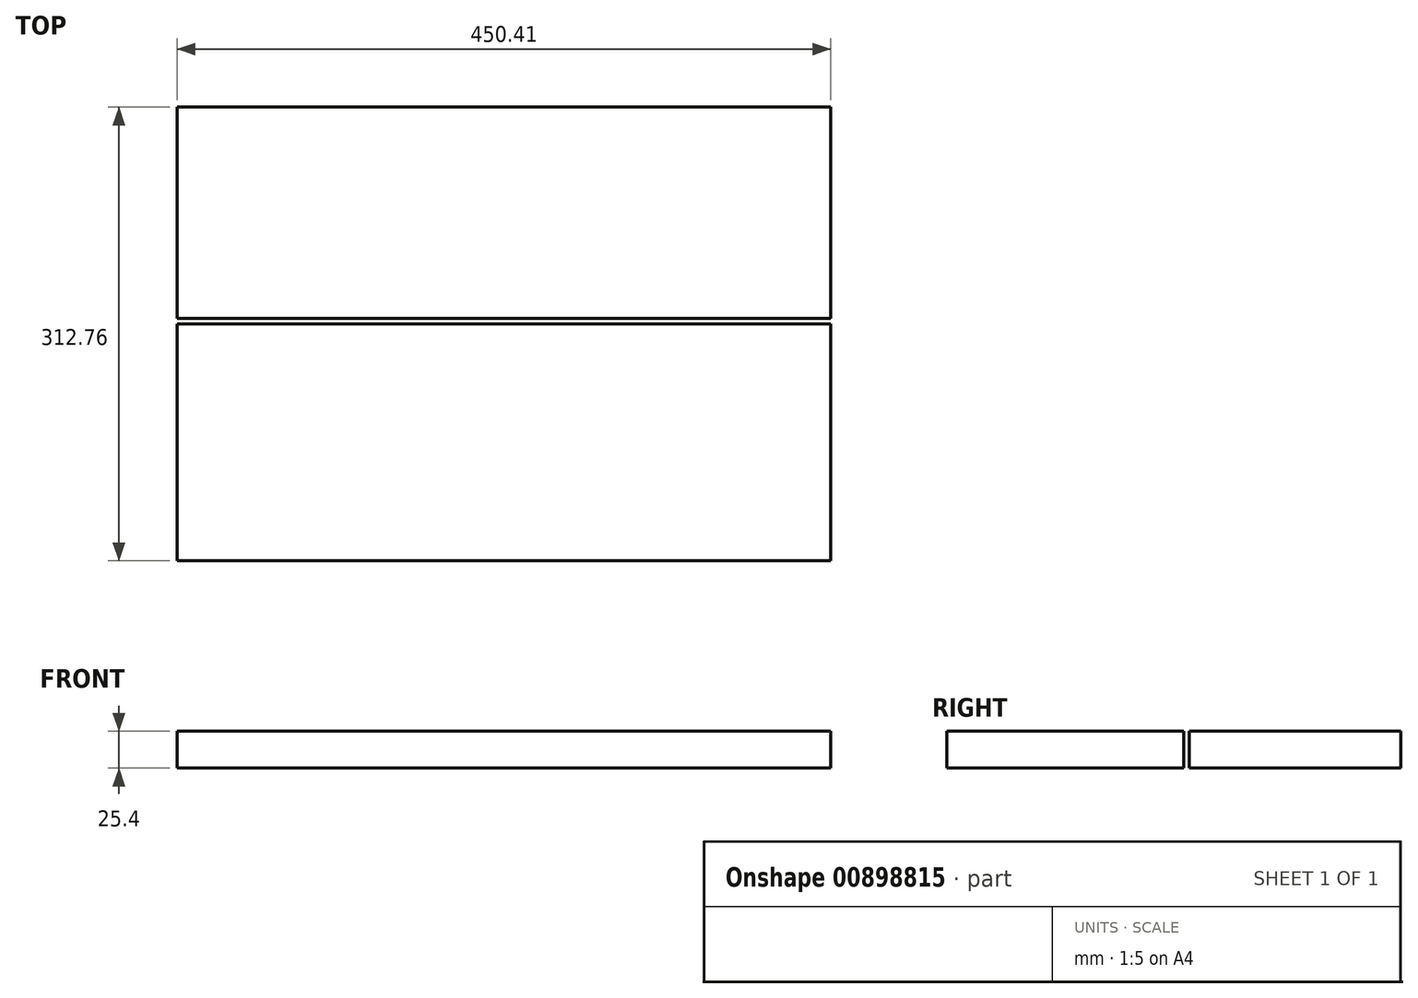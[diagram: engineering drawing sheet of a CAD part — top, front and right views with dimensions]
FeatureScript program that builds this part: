
annotation { "Feature Type Name" : "Feature", "Feature Type Description" : "" }
export const myFeature = defineFeature(function(context is Context, id is Id, definition is map)
    precondition{}
    {
        {
            var Q0;
            Q0=qCreatedBy(makeId("Top.planeOp"),FACE);
            var sketch = newSketch(context, id + "F0", { "sketchPlane" : qUnion([Q0])});
            skCircle(sketch, "E0", {"center": v(0, 0) * mm, "radius": 95.25 * mm});
            skCircle(sketch, "E1", {"center": v(0, 0) * mm, "radius": 85.73 * mm});
            skCircle(sketch, "E2", {"center": v(0, 0) * mm, "radius": 28.58 * mm});
            skSolve(sketch);
        }
        {
            var Q0;
            Q0=makeQuery(id+"F0.imprint","IMPRINT",FACE,{"disambiguationData":[TD([[makeQuery(id+"F0.imprint","IMPRINT",EDGE,{"derivedFrom":sQuery(id+"F0.wireOp",EDGE,"E0")}),1.0]])]});
            extrude(context, id + "F1", {"entities" : qUnion([Q0]), "depth" : 19.05 * mm, "offsetDistance" : 25.4 * mm});
        }
        {
            var Q0;
            Q0=makeQuery(id+"F0.imprint","IMPRINT",FACE,{"disambiguationData":[TD([[makeQuery(id+"F0.imprint","IMPRINT",EDGE,{"derivedFrom":sQuery(id+"F0.wireOp",EDGE,"E1")}),1.0]])]});
            var Q1;
            Q1=makeQuery(id+"F0.imprint","IMPRINT",FACE,{"disambiguationData":[TD([[makeQuery(id+"F0.imprint","IMPRINT",EDGE,{"derivedFrom":sQuery(id+"F0.wireOp",EDGE,"E2")}),1.0]])]});
            extrude(context, id + "F2", {"entities" : qUnion([Q0, Q1]), "operationType" : NewBodyOperationType.ADD, "depth" : 17.46 * mm, "offsetDistance" : 25.4 * mm});
        }
        {
            var Q0;
            Q0=makeQuery(id+"F0.imprint","IMPRINT",FACE,{"disambiguationData":[TD([[makeQuery(id+"F0.imprint","IMPRINT",EDGE,{"derivedFrom":sQuery(id+"F0.wireOp",EDGE,"E2")}),1.0]])]});
            var Q1;
            Q1=sQuery(id+"F0.wireOp",EDGE,"E2");
            extrude(context, id + "F3", {"entities" : qUnion([Q0]), "operationType" : NewBodyOperationType.ADD, "surfaceEntities" : qUnion([Q1]), "oppositeDirection" : true, "depth" : 25.4 * mm, "offsetDistance" : 25.4 * mm});
        }
        {
            var Q0;
            Q0=makeQuery(id+"F3.opExtrude","CAP_FACE",FACE,{"disambiguationData":[OSD([sQuery(id+"F0.wireOp",EDGE,"E2")])],"isStart":false});
            var sketch = newSketch(context, id + "F4", { "sketchPlane" : qUnion([Q0])});
            skLineSegment(sketch, "E3", {"start": v(165.45, 0) * mm, "end": v(165.45, -1.27) * mm});
            skLineSegment(sketch, "E4", {"start": v(165.45, -1.27) * mm, "end": v(165.45, 1.27) * mm});
            skLineSegment(sketch, "E5", {"start": v(165.45, -1.27) * mm, "end": v(-119.86, -1.27) * mm});
            skLineSegment(sketch, "E6", {"start": v(165.45, 1.27) * mm, "end": v(-119.86, 1.27) * mm});
            skLineSegment(sketch, "E7", {"start": v(-119.86, 1.27) * mm, "end": v(-119.86, -1.27) * mm});
            skSolve(sketch);
        }
        {
            var Q0;
            {var subQ0=sQuery(id+"F4.wireOp",EDGE,"E5");var subQ1=sQuery(id+"F4.wireOp",EDGE,"E4");var subQ2=makeQuery(id+"F4.imprint","INTERSECT",VERTEX,{"derivedFrom":[subQ1,subQ0]});Q0=makeQuery(id+"F4.imprint","IMPRINT",FACE,{"disambiguationData":[TD([[makeQuery(id+"F4.imprint","IMPRINT",EDGE,{"disambiguationData":[TD([[subQ2,-1.0]])],"derivedFrom":subQ1}),1.0]])]});}
            var Q1;
            {var subQ0=sQuery(id+"F4.wireOp",EDGE,"E5");var subQ1=makeQuery(id+"F3.opExtrude","CAP_EDGE",EDGE,{"disambiguationData":[OSD([sQuery(id+"F0.wireOp",EDGE,"E2")])],"isStart":false});var subQ2=makeQuery(id+"F4.imprint","INTERSECT",VERTEX,{"disambiguationData":[OD(0.0)],"derivedFrom":[subQ1,subQ0]});Q1=makeQuery(id+"F4.imprint","IMPRINT",FACE,{"disambiguationData":[TD([[makeQuery(id+"F4.imprint","IMPRINT",EDGE,{"disambiguationData":[TD([[subQ2,-1.0]])],"derivedFrom":subQ0}),-1.0]])]});}
            var Q2;
            {var subQ0=sQuery(id+"F4.wireOp",EDGE,"E7");Q2=makeQuery(id+"F4.imprint","IMPRINT",FACE,{"disambiguationData":[TD([[makeQuery(id+"F4.imprint","IMPRINT",EDGE,{"derivedFrom":subQ0}),1.0]])]});}
            extrude(context, id + "F5", {"entities" : qUnion([Q0, Q1, Q2]), "operationType" : NewBodyOperationType.REMOVE, "endBound" : BoundingType.THROUGH_ALL, "oppositeDirection" : true, "depth" : 25.4 * mm, "offsetDistance" : 25.4 * mm});
        }
        {
            var Q0;
            {var subQ0=sQuery(id+"F0.wireOp",EDGE,"E2");Q0=makeQuery(id+"F5.boolean.opBoolean","SPLIT",FACE,{"disambiguationData":[TD([makeQuery(id+"F5.opExtrude","SWEPT_FACE",FACE,{"disambiguationData":[OSD([sQuery(id+"F4.wireOp",EDGE,"E6")])]})])],"derivedFrom":makeQuery(id+"F3.opExtrude","CAP_FACE",FACE,{"disambiguationData":[OSD([subQ0])],"isStart":false})});}
            var sketch = newSketch(context, id + "F6", { "sketchPlane" : qUnion([Q0])});
            skPoint(sketch, "E8.firstSnap0", {"position": v(222.4, -8.28) * mm});
            skLineSegment(sketch, "E8.bottom", {"start": v(222.4, -148.24) * mm, "end": v(-228.02, -148.24) * mm});
            skLineSegment(sketch, "E8.top", {"start": v(222.4, 164.52) * mm, "end": v(-228.02, 164.52) * mm});
            skLineSegment(sketch, "E8.left", {"start": v(222.4, -148.24) * mm, "end": v(222.4, -2.57) * mm});
            skLineSegment(sketch, "E8.right", {"start": v(-228.02, -148.24) * mm, "end": v(-228.02, -2.57) * mm});
            skLineSegment(sketch, "E9", {"start": v(-228.02, 1.27) * mm, "end": v(222.4, 1.27) * mm});
            skPoint(sketch, "E9.endSnap0", {"position": v(222.4, 8.14) * mm});
            skLineSegment(sketch, "E10", {"start": v(222.4, -2.57) * mm, "end": v(-228.02, -2.57) * mm});
            skLineSegment(sketch, "E11.trimOffspring", {"start": v(-228.02, 1.27) * mm, "end": v(-228.02, 164.52) * mm});
            skLineSegment(sketch, "E12.trimOffspring", {"start": v(222.4, 1.27) * mm, "end": v(222.4, 164.52) * mm});
            skSolve(sketch);
        }
        {
            var Q0;
            Q0 = qSketchRegion(id + "F6", true);
            extrude(context, id + "F7", {"entities" : qUnion([Q0]), "depth" : 25.4 * mm, "offsetDistance" : 25.4 * mm});
        }
        {
            var Q0;
            Q0=makeQuery(id+"F5.boolean.opBoolean","SPLIT",BODY,{"disambiguationData":[OD(1.0)],"derivedFrom":makeQuery(id+"F1.opExtrude","SWEPT_BODY",BODY,{"disambiguationData":[OSD([sQuery(id+"F0.wireOp",EDGE,"E0"),sQuery(id+"F0.wireOp",EDGE,"E1")])]})});
            deleteBodies(context, id + "F8", {"entities" : qUnion([Q0])});
        }
    });
